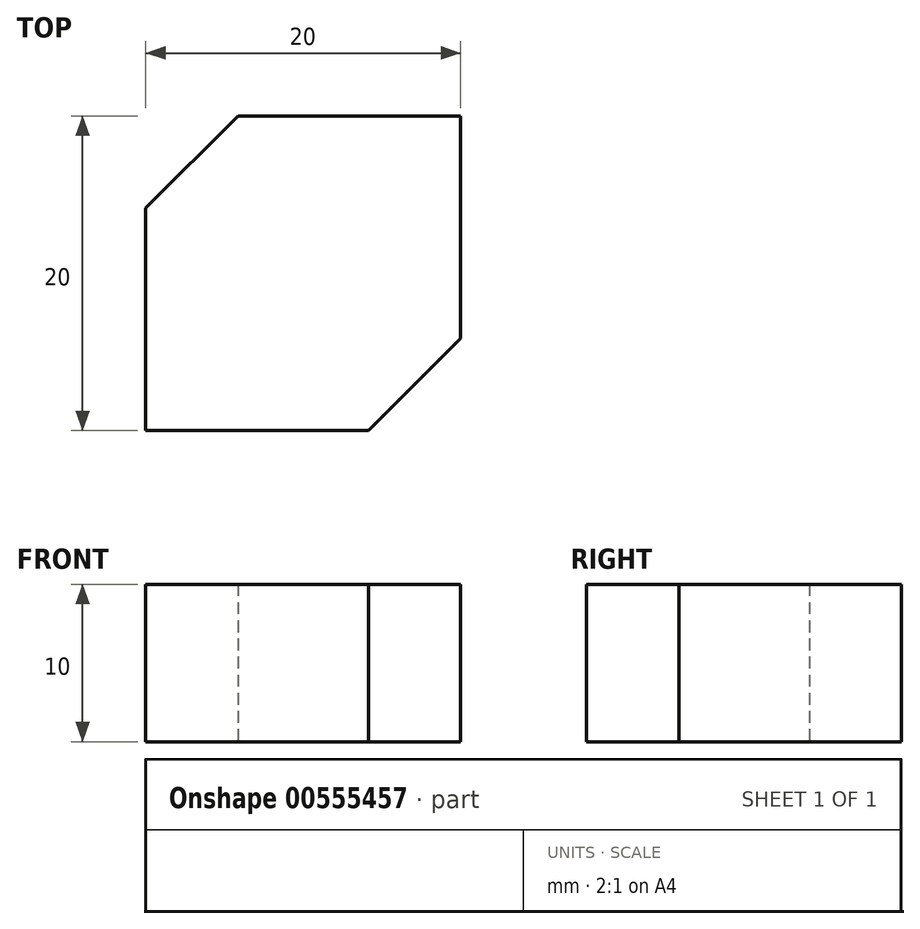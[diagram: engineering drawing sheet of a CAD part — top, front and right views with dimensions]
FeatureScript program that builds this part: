
annotation { "Feature Type Name" : "Feature", "Feature Type Description" : "" }
export const myFeature = defineFeature(function(context is Context, id is Id, definition is map)
    precondition{}
    {
        {
            var Q0;
            Q0=qCreatedBy(makeId("Top.planeOp"),FACE);
            var sketch = newSketch(context, id + "F0", { "sketchPlane" : qUnion([Q0])});
            skLineSegment(sketch, "E0.bottom", {"start": v(-10, 10) * mm, "end": v(-4.14, 10) * mm, "construction": true});
            skLineSegment(sketch, "E0.top", {"start": v(-10, -10) * mm, "end": v(4.14, -10) * mm});
            skLineSegment(sketch, "E0.left", {"start": v(-10, 10) * mm, "end": v(-10, 4.14) * mm, "construction": true});
            skLineSegment(sketch, "E0.right", {"start": v(10, 10) * mm, "end": v(10, -4.14) * mm});
            skPoint(sketch, "E0.middle", {"position": v(0, 0) * mm});
            skLineSegment(sketch, "E1", {"start": v(-10, 4.14) * mm, "end": v(-10, -10) * mm});
            skLineSegment(sketch, "E2", {"start": v(-4.14, 10) * mm, "end": v(10, 10) * mm});
            skLineSegment(sketch, "E3", {"start": v(10, -4.14) * mm, "end": v(10, -10) * mm, "construction": true});
            skLineSegment(sketch, "E4", {"start": v(4.14, -10) * mm, "end": v(10, -10) * mm, "construction": true});
            skLineSegment(sketch, "E5", {"start": v(-10, 4.14) * mm, "end": v(-4.14, 10) * mm});
            skLineSegment(sketch, "E6", {"start": v(10, -4.14) * mm, "end": v(4.14, -10) * mm});
            skSolve(sketch);
        }
        {
            var Q0;
            Q0=makeQuery(id+"F0.imprint","IMPRINT",FACE,{"disambiguationData":[TD([[makeQuery(id+"F0.imprint","IMPRINT",EDGE,{"derivedFrom":sQuery(id+"F0.wireOp",EDGE,"E0.top")}),1.0]])]});
            extrude(context, id + "F1", {"entities" : qUnion([Q0]), "depth" : 10 * mm, "offsetDistance" : 25 * mm});
        }
    });
